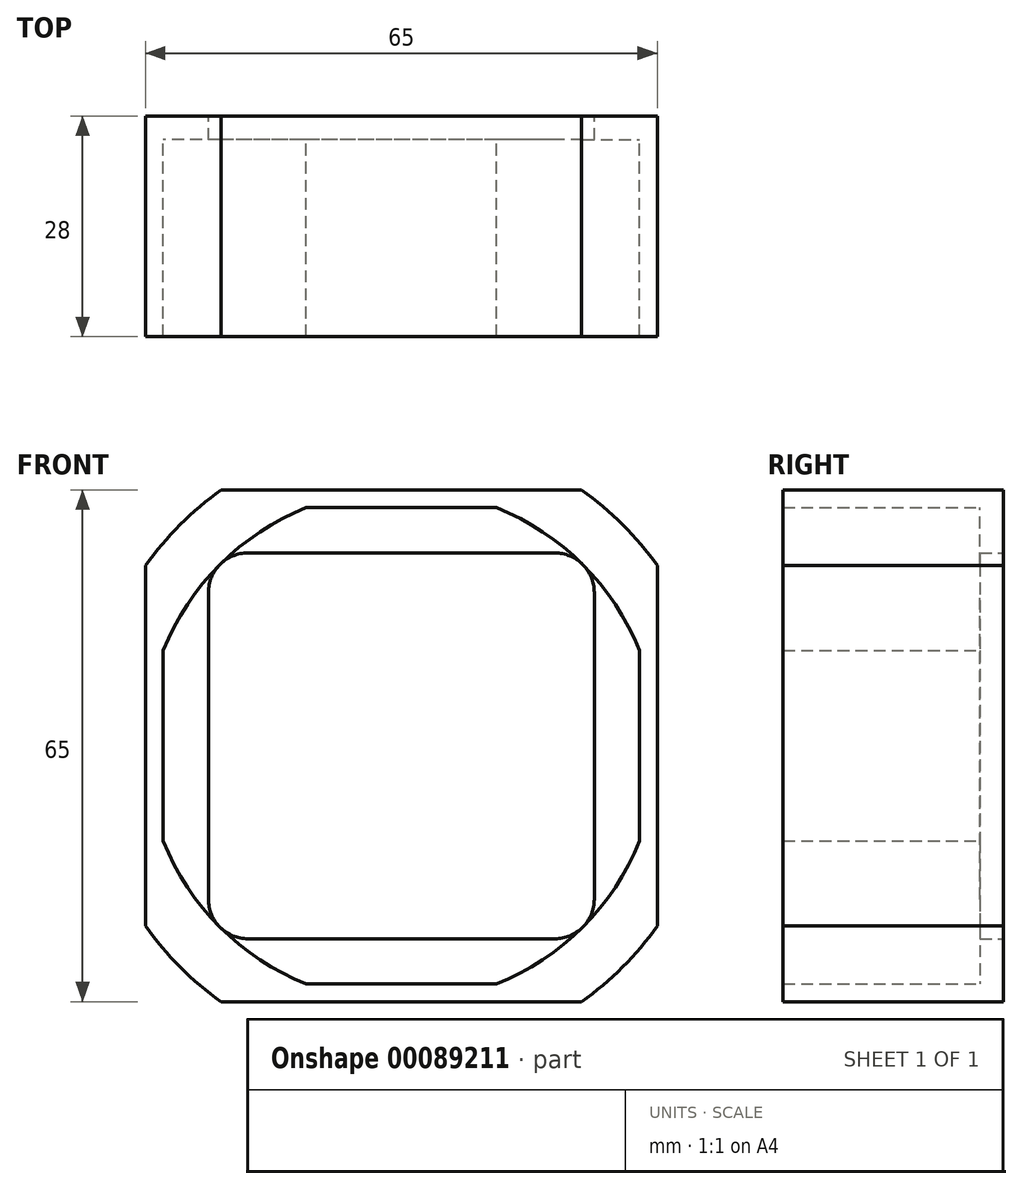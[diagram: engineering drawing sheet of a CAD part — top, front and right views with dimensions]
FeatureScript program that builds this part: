
annotation { "Feature Type Name" : "Feature", "Feature Type Description" : "" }
export const myFeature = defineFeature(function(context is Context, id is Id, definition is map)
    precondition{}
    {
        {
            var Q0;
            Q0=qCreatedBy(makeId("Front.planeOp"),FACE);
            var sketch = newSketch(context, id + "F0", { "sketchPlane" : qUnion([Q0])});
            skLineSegment(sketch, "E0.bottom", {"start": v(22.89, 32.5) * mm, "end": v(-22.89, 32.5) * mm});
            skLineSegment(sketch, "E0.top", {"start": v(22.89, -32.5) * mm, "end": v(-22.89, -32.5) * mm});
            skLineSegment(sketch, "E0.left", {"start": v(32.5, 22.89) * mm, "end": v(32.5, -22.89) * mm});
            skLineSegment(sketch, "E0.right", {"start": v(-32.5, 22.89) * mm, "end": v(-32.5, -22.89) * mm});
            skPoint(sketch, "E0.middle", {"position": v(0, 0) * mm});
            skArc(sketch, "E1", {"start": v(-22.89, 32.5) * mm, "mid": v(-28.1, 28.1) * mm, "end": v(-32.5, 22.89) * mm});
            skPoint(sketch, "E2.orphan", {"position": v(-32.5, 32.5) * mm});
            skArc(sketch, "E3.trimOffspring", {"start": v(-32.5, -22.89) * mm, "mid": v(-28.1, -28.1) * mm, "end": v(-22.89, -32.5) * mm});
            skPoint(sketch, "E4.orphan", {"position": v(-32.5, -32.5) * mm});
            skArc(sketch, "E5.trimOffspring", {"start": v(22.89, -32.5) * mm, "mid": v(28.1, -28.1) * mm, "end": v(32.5, -22.89) * mm});
            skPoint(sketch, "E6.orphan", {"position": v(32.5, -32.5) * mm});
            skArc(sketch, "E7.trimOffspring", {"start": v(32.5, 22.89) * mm, "mid": v(28.1, 28.1) * mm, "end": v(22.89, 32.5) * mm});
            skPoint(sketch, "E8.orphan", {"position": v(32.5, 32.5) * mm});
            skLineSegment(sketch, "E9.bottom", {"start": v(19.5, -24.5) * mm, "end": v(-19.5, -24.5) * mm});
            skLineSegment(sketch, "E9.top", {"start": v(19.5, 24.5) * mm, "end": v(-19.5, 24.5) * mm});
            skLineSegment(sketch, "E9.left", {"start": v(24.5, -19.5) * mm, "end": v(24.5, 19.5) * mm});
            skLineSegment(sketch, "E9.right", {"start": v(-24.5, -19.5) * mm, "end": v(-24.5, 19.5) * mm});
            skPoint(sketch, "E10.visualSharp", {"position": v(-24.5, 24.5) * mm});
            skArc(sketch, "E10.filletArc", {"start": v(-19.5, 24.5) * mm, "mid": v(-23.04, 23.04) * mm, "end": v(-24.5, 19.5) * mm});
            skPoint(sketch, "E11.visualSharp", {"position": v(24.5, 24.5) * mm});
            skArc(sketch, "E11.filletArc", {"start": v(24.5, 19.5) * mm, "mid": v(23.04, 23.04) * mm, "end": v(19.5, 24.5) * mm});
            skPoint(sketch, "E12.visualSharp", {"position": v(24.5, -24.5) * mm});
            skArc(sketch, "E12.filletArc", {"start": v(19.5, -24.5) * mm, "mid": v(23.04, -23.04) * mm, "end": v(24.5, -19.5) * mm});
            skPoint(sketch, "E13.visualSharp", {"position": v(-24.5, -24.5) * mm});
            skArc(sketch, "E13.filletArc", {"start": v(-24.5, -19.5) * mm, "mid": v(-23.04, -23.04) * mm, "end": v(-19.5, -24.5) * mm});
            skSolve(sketch);
        }
        {
            var Q0;
            Q0=makeQuery(id+"F0.imprint","IMPRINT",FACE,{"disambiguationData":[TD([[makeQuery(id+"F0.imprint","IMPRINT",EDGE,{"derivedFrom":sQuery(id+"F0.wireOp",EDGE,"E0.bottom")}),1.0]])]});
            extrude(context, id + "F1", {"entities" : qUnion([Q0]), "depth" : 3 * mm});
        }
        {
            var Q0;
            Q0=makeQuery(id+"F1.opExtrude","CAP_FACE",FACE,{"disambiguationData":[OSD([sQuery(id+"F0.wireOp",EDGE,"E0.bottom"),sQuery(id+"F0.wireOp",EDGE,"E0.top"),sQuery(id+"F0.wireOp",EDGE,"E0.left"),sQuery(id+"F0.wireOp",EDGE,"E0.right"),sQuery(id+"F0.wireOp",EDGE,"E1"),sQuery(id+"F0.wireOp",EDGE,"E3.trimOffspring"),sQuery(id+"F0.wireOp",EDGE,"E5.trimOffspring"),sQuery(id+"F0.wireOp",EDGE,"E7.trimOffspring"),sQuery(id+"F0.wireOp",EDGE,"E9.bottom"),sQuery(id+"F0.wireOp",EDGE,"E9.top"),sQuery(id+"F0.wireOp",EDGE,"E9.left"),sQuery(id+"F0.wireOp",EDGE,"E9.right"),sQuery(id+"F0.wireOp",EDGE,"E10.filletArc"),sQuery(id+"F0.wireOp",EDGE,"E11.filletArc"),sQuery(id+"F0.wireOp",EDGE,"E12.filletArc"),sQuery(id+"F0.wireOp",EDGE,"E13.filletArc")])],"isStart":false});
            var sketch = newSketch(context, id + "F2", { "sketchPlane" : qUnion([Q0])});
            skLineSegment(sketch, "E14.bottom", {"start": v(12.1, 30.25) * mm, "end": v(-12.1, 30.25) * mm});
            skLineSegment(sketch, "E14.top", {"start": v(12.1, -30.25) * mm, "end": v(-12.1, -30.25) * mm});
            skLineSegment(sketch, "E14.left", {"start": v(30.25, 12.1) * mm, "end": v(30.25, -12.1) * mm});
            skLineSegment(sketch, "E14.right", {"start": v(-30.25, 12.1) * mm, "end": v(-30.25, -12.1) * mm});
            skPoint(sketch, "E14.middle", {"position": v(0, 0) * mm});
            skArc(sketch, "E15", {"start": v(-12.1, 30.25) * mm, "mid": v(-23.04, 23.04) * mm, "end": v(-30.25, 12.1) * mm});
            skPoint(sketch, "E16.orphan", {"position": v(-30.25, 30.25) * mm});
            skPoint(sketch, "E17.orphan", {"position": v(30.25, 30.25) * mm});
            skArc(sketch, "E18.trimOffspring", {"start": v(30.25, 12.1) * mm, "mid": v(23.04, 23.04) * mm, "end": v(12.1, 30.25) * mm});
            skPoint(sketch, "E19.orphan", {"position": v(30.25, -30.25) * mm});
            skArc(sketch, "E20.trimOffspring", {"start": v(12.1, -30.25) * mm, "mid": v(23.04, -23.04) * mm, "end": v(30.25, -12.1) * mm});
            skPoint(sketch, "E21.orphan", {"position": v(-30.25, -30.25) * mm});
            skArc(sketch, "E22.trimOffspring", {"start": v(-30.25, -12.1) * mm, "mid": v(-23.04, -23.04) * mm, "end": v(-12.1, -30.25) * mm});
            skSolve(sketch);
        }
        {
            var Q0;
            {var subQ4=sQuery(id+"F2.wireOp",EDGE,"E14.bottom");Q0=makeQuery(id+"F2.imprint","IMPRINT",FACE,{"disambiguationData":[TD([[makeQuery(id+"F2.imprint","IMPRINT",EDGE,{"derivedFrom":subQ4}),-1.0]])]});}
            extrude(context, id + "F3", {"entities" : qUnion([Q0]), "operationType" : NewBodyOperationType.ADD, "depth" : 25 * mm});
        }
    });
